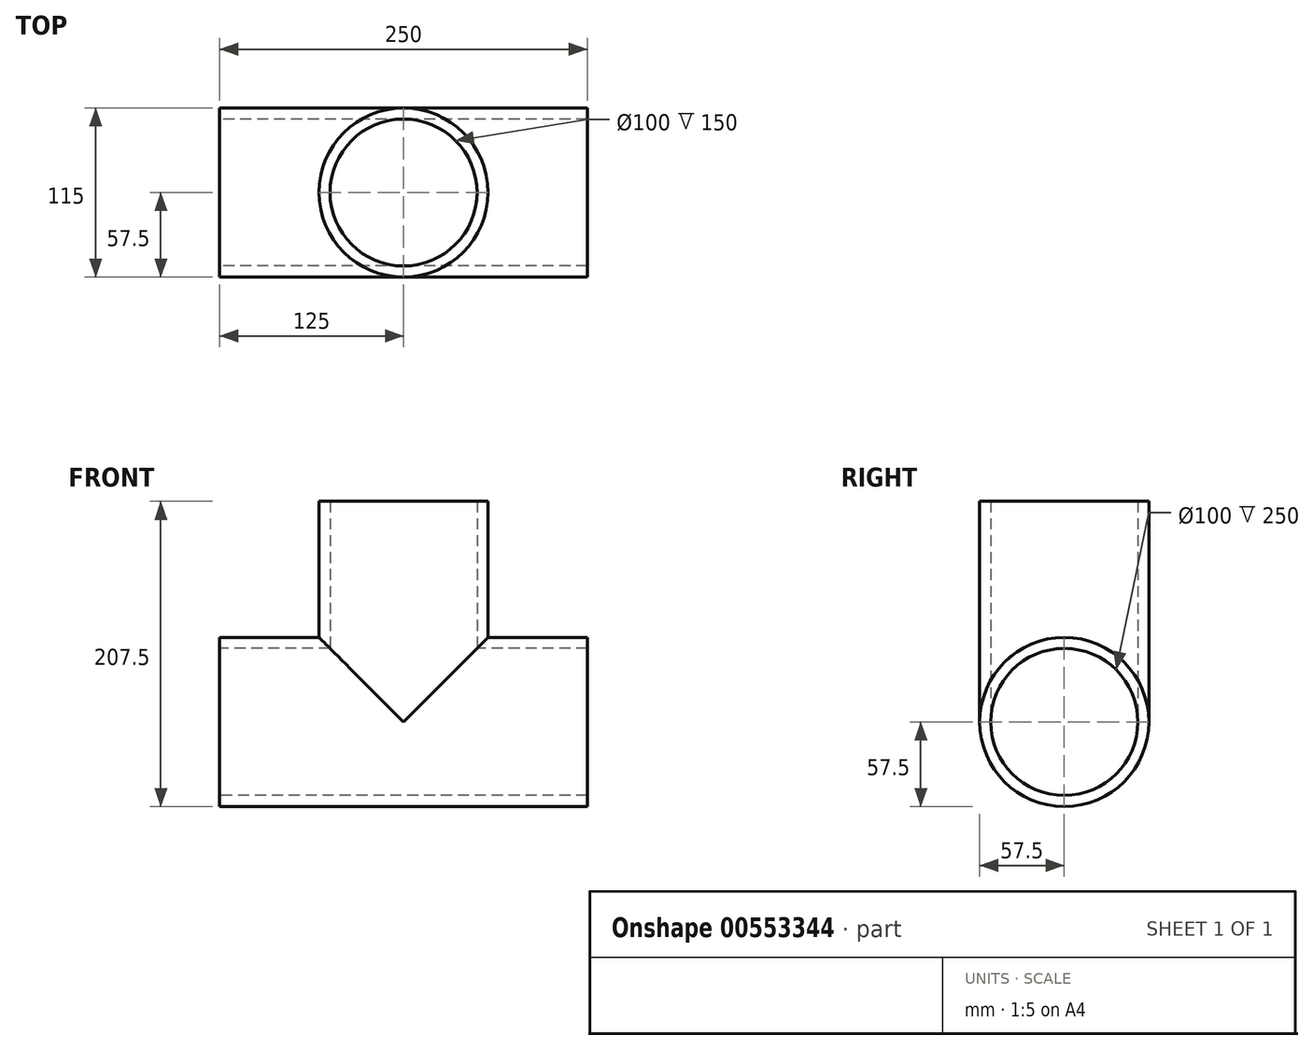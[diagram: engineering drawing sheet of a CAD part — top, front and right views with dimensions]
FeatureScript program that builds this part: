
annotation { "Feature Type Name" : "Feature", "Feature Type Description" : "" }
export const myFeature = defineFeature(function(context is Context, id is Id, definition is map)
    precondition{}
    {
        {
            var Q0;
            Q0=qCreatedBy(makeId("Right.planeOp"),FACE);
            var sketch = newSketch(context, id + "F0", { "sketchPlane" : qUnion([Q0])});
            skCircle(sketch, "E0", {"center": v(0, 0) * mm, "radius": 57.5 * mm});
            skCircle(sketch, "E1", {"center": v(0, 0) * mm, "radius": 50 * mm});
            skSolve(sketch);
        }
        {
            var Q0;
            Q0=makeQuery(id+"F0.imprint","IMPRINT",FACE,{"disambiguationData":[TD([[makeQuery(id+"F0.imprint","IMPRINT",EDGE,{"derivedFrom":sQuery(id+"F0.wireOp",EDGE,"E0")}),1.0]])]});
            extrude(context, id + "F1", {"entities" : qUnion([Q0]), "endBound" : BoundingType.SYMMETRIC, "depth" : 250 * mm, "offsetDistance" : 25 * mm});
        }
        {
            var Q0;
            Q0=qCreatedBy(makeId("Top.planeOp"),FACE);
            var sketch = newSketch(context, id + "F2", { "sketchPlane" : qUnion([Q0])});
            skCircle(sketch, "E2", {"center": v(0, 0) * mm, "radius": 57.5 * mm});
            skCircle(sketch, "E3", {"center": v(0, 0) * mm, "radius": 50 * mm});
            skSolve(sketch);
        }
        {
            var Q0;
            Q0 = qSketchRegion(id + "F2", true);
            extrude(context, id + "F3", {"entities" : qUnion([Q0]), "operationType" : NewBodyOperationType.ADD, "depth" : 150 * mm, "offsetDistance" : 25 * mm});
        }
        {
            var Q0;
            Q0=makeQuery(id+"F1.opExtrude","CAP_FACE",FACE,{"disambiguationData":[OSD([sQuery(id+"F0.wireOp",EDGE,"E0"),sQuery(id+"F0.wireOp",EDGE,"E1")])],"isStart":true});
            var sketch = newSketch(context, id + "F4", { "sketchPlane" : qUnion([Q0])});
            skCircle(sketch, "E4.0", {"center": v(0, 0) * mm, "radius": 50 * mm});
            skSolve(sketch);
        }
        {
            var Q0;
            Q0 = qSketchRegion(id + "F4", true);
            extrude(context, id + "F5", {"entities" : qUnion([Q0]), "operationType" : NewBodyOperationType.REMOVE, "oppositeDirection" : true, "depth" : 250 * mm, "offsetDistance" : 25 * mm});
        }
        {
            var Q0;
            Q0=makeQuery(id+"F3.opExtrude","CAP_FACE",FACE,{"disambiguationData":[OSD([sQuery(id+"F2.wireOp",EDGE,"E2"),sQuery(id+"F2.wireOp",EDGE,"E3")])],"isStart":false});
            var sketch = newSketch(context, id + "F6", { "sketchPlane" : qUnion([Q0])});
            skCircle(sketch, "E5.0", {"center": v(0, 0) * mm, "radius": 50 * mm});
            skSolve(sketch);
        }
        {
            var Q0;
            Q0=makeQuery(id+"F6.imprint","IMPRINT",FACE,{"disambiguationData":[TD([[makeQuery(id+"F6.imprint","IMPRINT",EDGE,{"derivedFrom":sQuery(id+"F6.wireOp",EDGE,"E5.0")}),1.0]])]});
            extrude(context, id + "F7", {"entities" : qUnion([Q0]), "operationType" : NewBodyOperationType.REMOVE, "oppositeDirection" : true, "depth" : 150 * mm, "offsetDistance" : 25 * mm});
        }
    });
